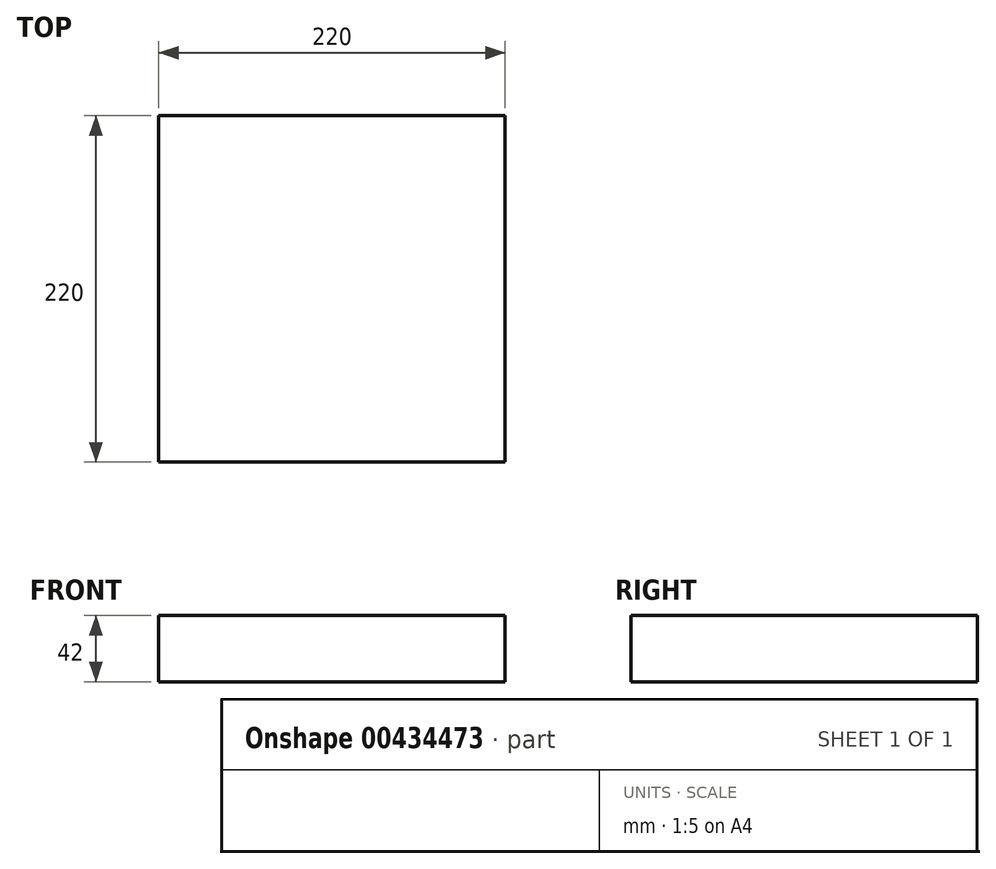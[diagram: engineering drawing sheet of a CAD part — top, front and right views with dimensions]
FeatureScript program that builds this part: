
annotation { "Feature Type Name" : "Feature", "Feature Type Description" : "" }
export const myFeature = defineFeature(function(context is Context, id is Id, definition is map)
    precondition{}
    {
        {
            var Q0;
            Q0=qCreatedBy(makeId("Top.planeOp"),FACE);
            var sketch = newSketch(context, id + "F0", { "sketchPlane" : qUnion([Q0])});
            skLineSegment(sketch, "E0.bottom", {"start": v(110, 110) * mm, "end": v(-110, 110) * mm});
            skLineSegment(sketch, "E0.top", {"start": v(110, -110) * mm, "end": v(-110, -110) * mm});
            skLineSegment(sketch, "E0.left", {"start": v(110, 110) * mm, "end": v(110, -110) * mm});
            skLineSegment(sketch, "E0.right", {"start": v(-110, 110) * mm, "end": v(-110, -110) * mm});
            skPoint(sketch, "E0.middle", {"position": v(0, 0) * mm});
            skSolve(sketch);
        }
        {
            var Q0;
            Q0 = qSketchRegion(id + "F0", true);
            extrude(context, id + "F1", {"entities" : qUnion([Q0]), "depth" : 42 * mm});
        }
    });
